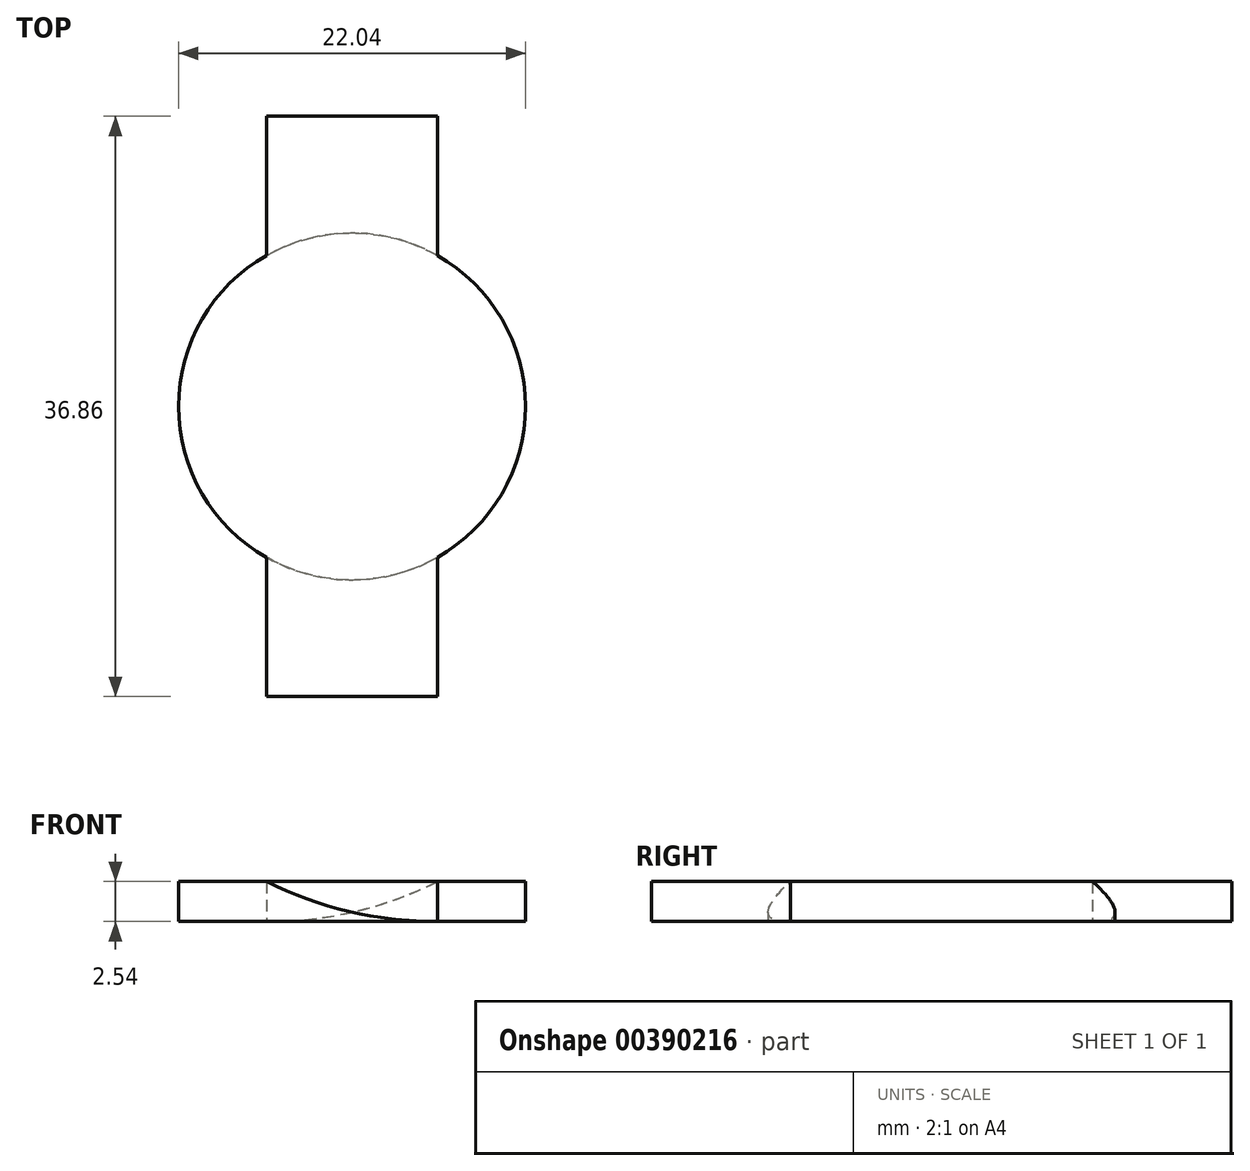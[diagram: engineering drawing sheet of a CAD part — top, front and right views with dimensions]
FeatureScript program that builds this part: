
annotation { "Feature Type Name" : "Feature", "Feature Type Description" : "" }
export const myFeature = defineFeature(function(context is Context, id is Id, definition is map)
    precondition{}
    {
        {
            var Q0;
            Q0=qCreatedBy(makeId("Top.planeOp"),FACE);
            var sketch = newSketch(context, id + "F0", { "sketchPlane" : qUnion([Q0])});
            skCircle(sketch, "E0", {"center": v(0, 0) * mm, "radius": 11.02 * mm});
            skLineSegment(sketch, "E1.bottom", {"start": v(5.42, 18.43) * mm, "end": v(-5.42, 18.43) * mm});
            skLineSegment(sketch, "E1.top", {"start": v(5.42, -18.43) * mm, "end": v(-5.42, -18.43) * mm});
            skLineSegment(sketch, "E1.left", {"start": v(5.42, 18.43) * mm, "end": v(5.42, -18.43) * mm});
            skLineSegment(sketch, "E1.right", {"start": v(-5.42, 18.43) * mm, "end": v(-5.42, -18.43) * mm});
            skSolve(sketch);
        }
        {
            var Q0;
            Q0=qSketchRegion(id+"F0",true);
            extrude(context, id + "F1", {"entities" : qUnion([Q0]), "depth" : 2.54 * mm});
        }
        {
            var Q0;
            {var subQ0=sQuery(id+"F0.wireOp",EDGE,"E1.right");Q0=makeQuery(id+"F1.opExtrude","CAP_EDGE",EDGE,{"disambiguationData":[OSD([subQ0]),TDD([makeQuery(id+"F0.imprint","IMPRINT",EDGE,{"disambiguationData":[TD([[makeQuery(id+"F0.imprint","INTERSECT",VERTEX,{"derivedFrom":[sQuery(id+"F0.wireOp",EDGE,"E1.top"),subQ0]}),1.0]])],"derivedFrom":subQ0})])],"isStart":true});}
            var Q1;
            {var subQ0=sQuery(id+"F0.wireOp",EDGE,"E1.left");Q1=makeQuery(id+"F1.opExtrude","CAP_EDGE",EDGE,{"disambiguationData":[OSD([subQ0]),TDD([makeQuery(id+"F0.imprint","IMPRINT",EDGE,{"disambiguationData":[TD([[makeQuery(id+"F0.imprint","INTERSECT",VERTEX,{"derivedFrom":[sQuery(id+"F0.wireOp",EDGE,"E1.bottom"),subQ0]}),-1.0]])],"derivedFrom":subQ0})])],"isStart":true});}
            fillet(context, id + "F2", {"entities" : qUnion([Q0, Q1]), "radius" : 23.92 * mm, "tangentPropagation" : true, "allowEdgeOverflow" : false});
        }
    });
